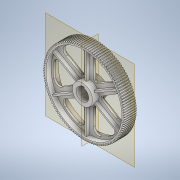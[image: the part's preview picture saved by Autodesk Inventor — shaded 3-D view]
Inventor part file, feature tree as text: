
AUTODESK INVENTOR PART (.ipt)
format: ipt  version: 2020 (Build 240168000, 168)  size: 1,957,376 bytes
history: native  units: mm (DEFAULTED — no unit token found)
features: sketch x9, extrude x7, plane x7, other x6, pattern_circular x2, projected_geometry x2, loft x1, revolve x1, mirror x1
ambient origin geometry x8: Origin, YZ Plane, XZ Plane, XY Plane, X Axis, Y Axis, Z Axis, Center Point
bodies: Solid1 (feature_tree), 实体2 (feature_tree)
feature tree (36):
  extrude  "Extrusion1"  Depth=73.0mm TaperAngle=0.0deg
  plane  "Work Plane2"
  plane  "Work Plane8"
  plane  "Work Plane9"
  other  "正齿轮"
  sketch  "草图3"  dims[d16=276.0mm d17=0.0mm d34=0.263999mm]
  extrude  "拉伸2"  Depth=10.0mm TaperAngle=0.0deg
  extrude  "拉伸9"  Depth=0.263999mm TaperAngle=0.0deg
  plane  "工作平面11"
  sketch  "草图5"  dims[d39=0.0mm d41=0.0mm]
  extrude  "拉伸4"  TaperAngle=0.0deg  [1 undecoded]
  plane  "工作平面12"
  loft  "放样1"
  extrude  "拉伸5"  Depth=75.0mm
  other  "合并1"
  pattern_circular  "环形阵列1"  Count=12  [1 undecoded]
  extrude  "拉伸10"  Depth=20.0mm
  extrude  "拉伸11"  Depth=5.0mm
  pattern_circular  "环形阵列3"  [2 undecoded]
  plane  "工作平面13"
  plane  "工作平面14"
  sketch  "草图10"  dims[d56=81.5mm d57=0.0mm d68=59.0mm d69=10.0mm d70=53.0mm d71=12.0mm d72=60.0mm d73=476.0mm d74=452.0mm d75=0.0mm d76=0.0mm d77=227.0mm d78=12.0mm d79=48.0mm d80=10.0mm d81=53.0mm d82=36.5mm d83=0.0mm d84=90.0deg d85=0.0mm d86=90.0deg d87=10.0mm d88=0.0mm d89=20.0mm d91=90.0deg d99=10.0mm d100=0.0mm d101=60.0mm d102=360.0deg d104=10.0mm d105=0.0mm d109=428.0mm d110=144.0mm d111=60.0mm d112=60.0mm d114=10.0mm d115=10.0mm d116=10.0mm d117=0.0mm d118=60.0mm d119=360.0deg d124=2.0mm d125=2.0mm d126=90.0deg d113=0.5mm]
  other  "工作轴1"
  revolve  "旋转2"  [1 undecoded]
  mirror  "镜像1"
  sketch  "Sketch1"  dims[d0=484.0mm d1=73.0mm d2=0.0mm]
  sketch  "Sketch2"  dims[d3=476.0mm d4=10.0mm d5=0.0mm]
  other  "Srf1"
  projected_geometry  "投影回路1"
  sketch  "草图6"  dims[d43=276.0mm d46=276.0mm]
  sketch  "草图7"  dims[d47=0.0mm d48=0.0mm d49=75.0mm d50=120.0mm]
  sketch  "草图8"  dims[d51=8.5mm d52=0.0mm d53=20.0mm]
  sketch  "草图9"  dims[d54=12.0mm d55=5.0mm]
  projected_geometry  "投影回路2"
  other  "投影剖切边1"
  other  "投影剖切边2"
note: 5 required parameter values undecoded (feature->parameter linkage not recoverable at this tier; creation-order binding heuristic only, values carry confidence <= 0.55)